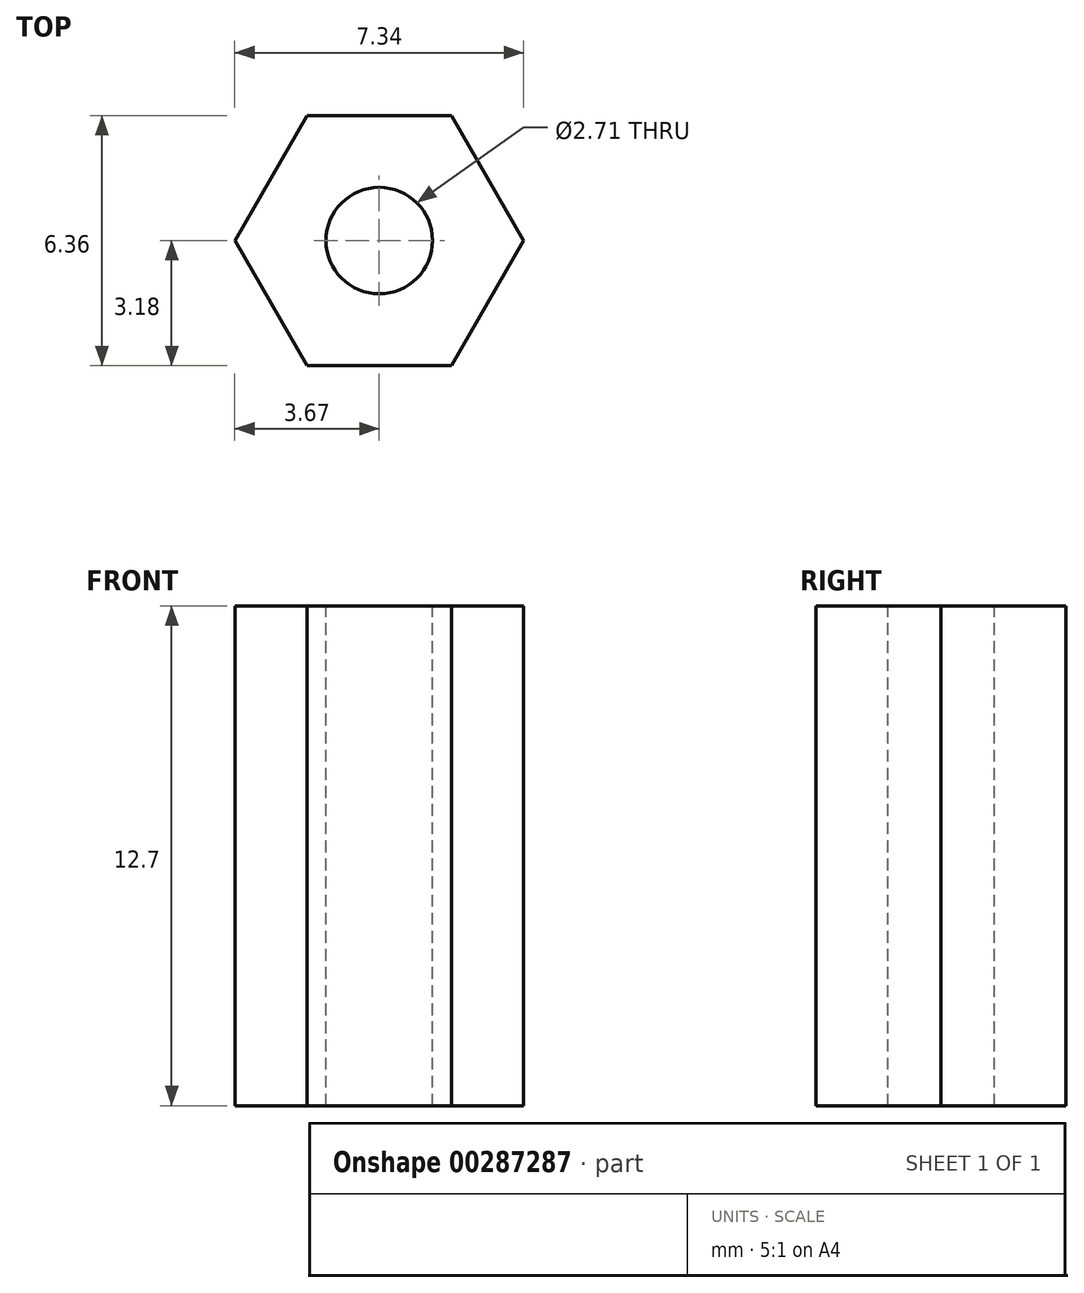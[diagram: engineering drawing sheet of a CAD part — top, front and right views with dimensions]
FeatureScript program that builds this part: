
annotation { "Feature Type Name" : "Feature", "Feature Type Description" : "" }
export const myFeature = defineFeature(function(context is Context, id is Id, definition is map)
    precondition{}
    {
        {
            var Q0;
            Q0=qCreatedBy(makeId("Top.planeOp"),FACE);
            var sketch = newSketch(context, id + "F0", { "sketchPlane" : qUnion([Q0])});
            skCircle(sketch, "E0.cCircle", {"center": v(0, 0) * mm, "radius": 3.18 * mm, "construction": true});
            skLineSegment(sketch, "E0.0", {"start": v(3.67, 0) * mm, "end": v(1.83, -3.18) * mm});
            skLineSegment(sketch, "E0.1", {"start": v(1.83, -3.18) * mm, "end": v(-1.83, -3.18) * mm});
            skLineSegment(sketch, "E0.2", {"start": v(-1.83, -3.18) * mm, "end": v(-3.67, 0) * mm});
            skLineSegment(sketch, "E0.3", {"start": v(-3.67, 0) * mm, "end": v(-1.83, 3.17) * mm});
            skLineSegment(sketch, "E0.4", {"start": v(-1.83, 3.18) * mm, "end": v(1.83, 3.18) * mm});
            skLineSegment(sketch, "E0.5", {"start": v(1.83, 3.18) * mm, "end": v(3.67, 0) * mm});
            skPoint(sketch, "E0.0.midPoint", {"position": v(3.18, 0) * mm});
            skSolve(sketch);
        }
        {
            var Q0;
            Q0 = qSketchRegion(id + "F0", true);
            extrude(context, id + "F1", {"entities" : qUnion([Q0]), "depth" : 12.7 * mm});
        }
        {
            var Q0;
            Q0=makeQuery(id+"F1.opExtrude","CAP_FACE",FACE,{"disambiguationData":[OSD([sQuery(id+"F0.wireOp",EDGE,"E0.0"),sQuery(id+"F0.wireOp",EDGE,"E0.1"),sQuery(id+"F0.wireOp",EDGE,"E0.2"),sQuery(id+"F0.wireOp",EDGE,"E0.3"),sQuery(id+"F0.wireOp",EDGE,"E0.4"),sQuery(id+"F0.wireOp",EDGE,"E0.5")])],"isStart":false});
            var sketch = newSketch(context, id + "F2", { "sketchPlane" : qUnion([Q0])});
            skPoint(sketch, "E1", {"position": v(0, 0) * mm});
            skSolve(sketch);
        }
        {
            var Q0;
            Q0=sQuery(id+"F2.wireOp",VERTEX,"E1");
            var Q1;
            Q1=makeQuery(id+"F1.opExtrude","SWEPT_BODY",BODY,{"disambiguationData":[OSD([sQuery(id+"F0.wireOp",EDGE,"E0.0"),sQuery(id+"F0.wireOp",EDGE,"E0.1"),sQuery(id+"F0.wireOp",EDGE,"E0.2"),sQuery(id+"F0.wireOp",EDGE,"E0.3"),sQuery(id+"F0.wireOp",EDGE,"E0.4"),sQuery(id+"F0.wireOp",EDGE,"E0.5")])]});
            hole(context, id + "F3", {"style" : HoleStyle.SIMPLE, "endStyle" : HoleEndStyle.THROUGH, "standardTappedOrClearance" : lookupTablePath({ "standard" : "ANSI", "engagement" : "75%", "pitch" : "32 tpi", "size" : "#6", "type" : "Tapped" }), "standardBlindInLast" : lookupTablePath({ "standard" : "ANSI", "engagement" : "75%", "pitch" : "32 tpi", "size" : "#6", "type" : "Tapped" }), "holeDiameter" : 2.7 * mm, "showTappedDepth" : true, "tappedDepth" : 2.77 * mm, "tapClearance" : 3, "startFromSketch" : true, "locations" : qUnion([Q0]), "scope" : qUnion([Q1]), "majorDiameter" : 3.5 * mm});
        }
    });
